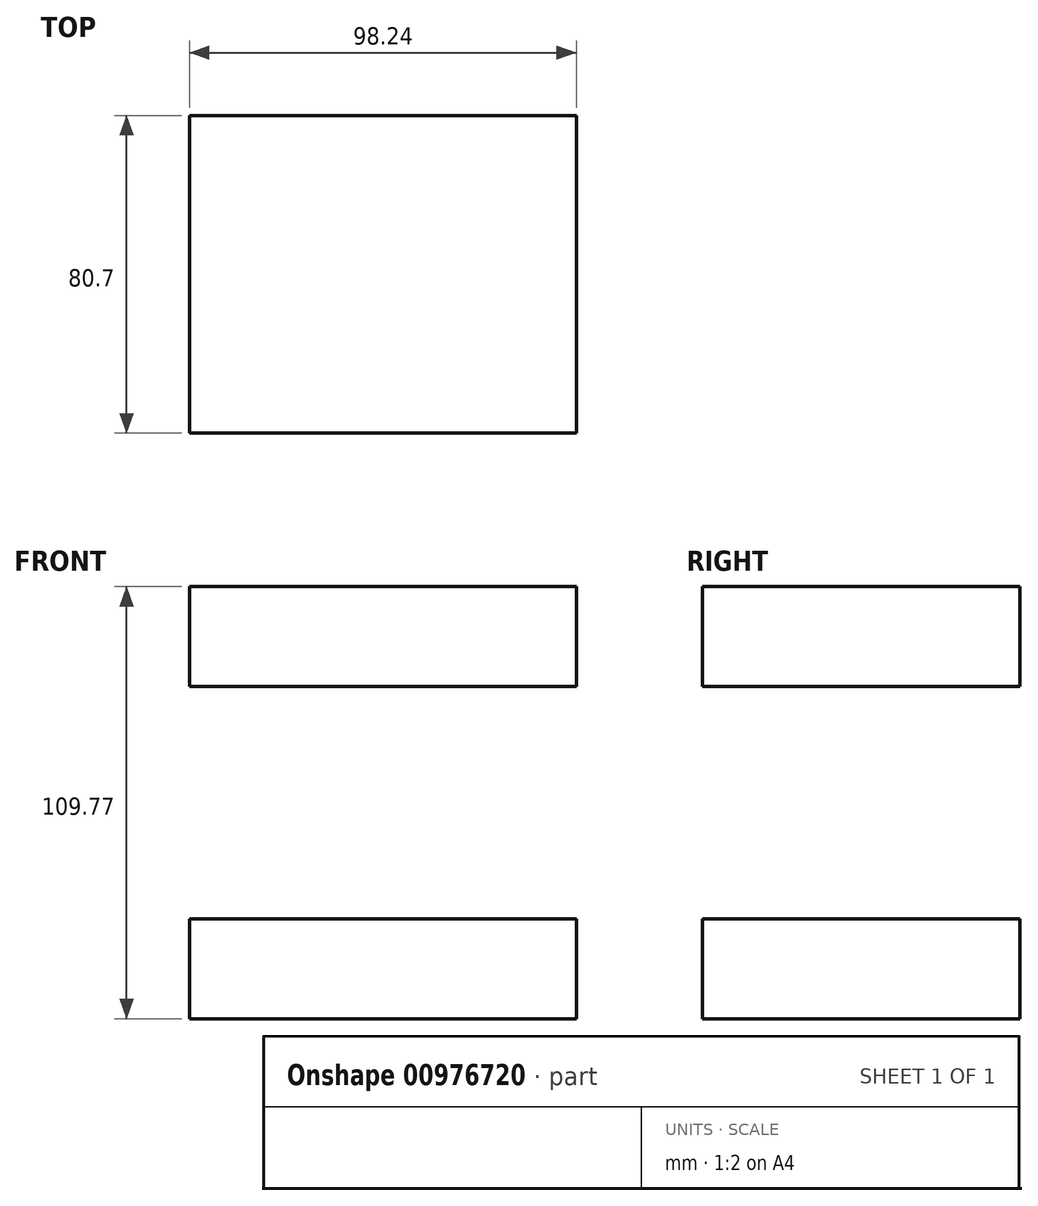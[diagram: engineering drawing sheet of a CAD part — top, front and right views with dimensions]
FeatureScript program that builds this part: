
annotation { "Feature Type Name" : "Feature", "Feature Type Description" : "" }
export const myFeature = defineFeature(function(context is Context, id is Id, definition is map)
    precondition{}
    {
        {
            var Q0;
            Q0=qCreatedBy(makeId("Top.planeOp"),FACE);
            var sketch = newSketch(context, id + "F0", { "sketchPlane" : qUnion([Q0])});
            skLineSegment(sketch, "E0.bottom", {"start": v(-40.34, 37.12) * mm, "end": v(57.9, 37.12) * mm});
            skLineSegment(sketch, "E0.top", {"start": v(-40.34, -43.58) * mm, "end": v(57.9, -43.58) * mm});
            skLineSegment(sketch, "E0.left", {"start": v(-40.34, 37.12) * mm, "end": v(-40.34, -43.58) * mm});
            skLineSegment(sketch, "E0.right", {"start": v(57.9, 37.12) * mm, "end": v(57.9, -43.58) * mm});
            skSolve(sketch);
        }
        {
            var Q0;
            Q0=makeQuery(id+"F0.imprint","IMPRINT",FACE,{"disambiguationData":[TD([[makeQuery(id+"F0.imprint","IMPRINT",EDGE,{"derivedFrom":sQuery(id+"F0.wireOp",EDGE,"E0.bottom")}),-1.0]])]});
            extrude(context, id + "F1", {"entities" : qUnion([Q0]), "depth" : 25.4 * mm, "offsetDistance" : 25.4 * mm});
        }
        {
            var Q0;
            Q0=makeQuery(id+"F1.opExtrude","SWEPT_BODY",BODY,{"disambiguationData":[OSD([sQuery(id+"F0.wireOp",EDGE,"E0.bottom"),sQuery(id+"F0.wireOp",EDGE,"E0.top"),sQuery(id+"F0.wireOp",EDGE,"E0.left"),sQuery(id+"F0.wireOp",EDGE,"E0.right")])]});
            transform(context, id + "F2", {"entities" : qUnion([Q0]), "transformType" : TransformType.COPY});
        }
        {
            var Q0;
            Q0=makeQuery(id+"F1.opExtrude","SWEPT_BODY",BODY,{"disambiguationData":[OSD([sQuery(id+"F0.wireOp",EDGE,"E0.bottom"),sQuery(id+"F0.wireOp",EDGE,"E0.top"),sQuery(id+"F0.wireOp",EDGE,"E0.left"),sQuery(id+"F0.wireOp",EDGE,"E0.right")])]});
            transform(context, id + "F3", {"entities" : qUnion([Q0]), "transformType" : TransformType.TRANSLATION_3D, "dx" : 0 * mm, "dy" : 0 * mm, "dz" : 84.37 * mm, "makeCopy" : false});
        }
    });
